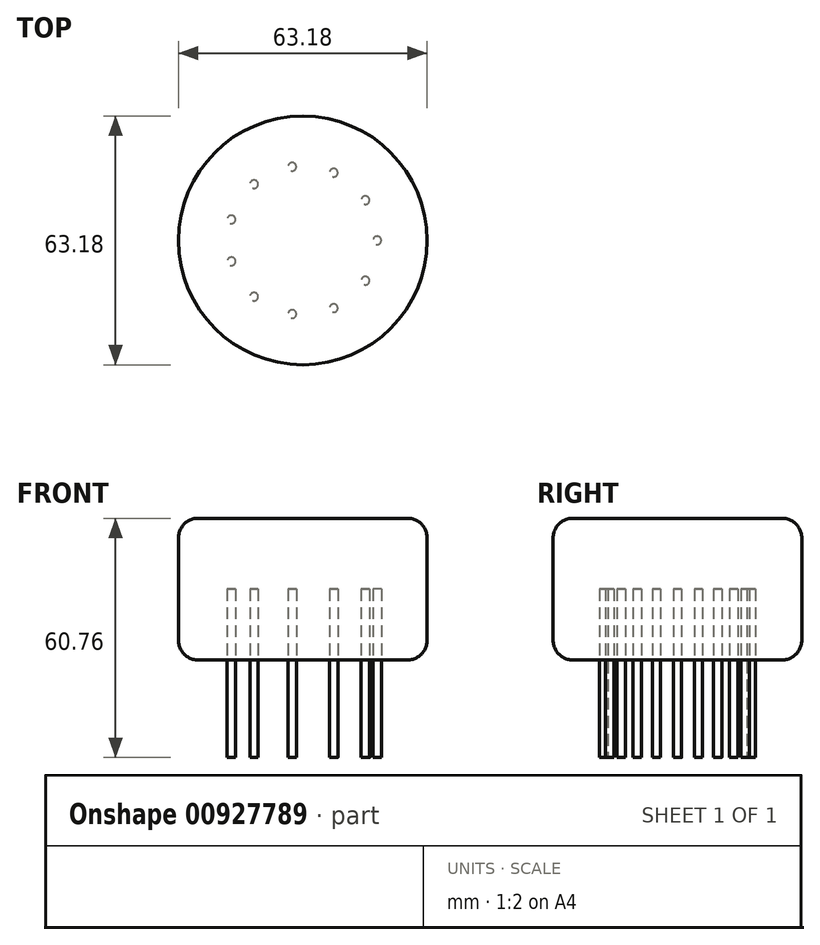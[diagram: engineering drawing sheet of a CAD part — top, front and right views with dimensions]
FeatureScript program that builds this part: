
annotation { "Feature Type Name" : "Feature", "Feature Type Description" : "" }
export const myFeature = defineFeature(function(context is Context, id is Id, definition is map)
    precondition{}
    {
        {
            var Q0;
            Q0=qCreatedBy(makeId("Front.planeOp"),FACE);
            var sketch = newSketch(context, id + "F0", { "sketchPlane" : qUnion([Q0])});
            skLineSegment(sketch, "E0", {"start": v(18.6, 87.25) * mm, "end": v(18.6, 44.5) * mm});
            skSolve(sketch);
        }
        {
            var Q0;
            Q0=qCreatedBy(makeId("Top.planeOp"),FACE);
            var Q1;
            Q1=qBodyType(qCreatedBy(id+"F2",EDGE),BodyType.WIRE);
            cPlane(context, id + "F1", {"entities" : qUnion([Q0, Q1]), "cplaneType" : CPlaneType.OFFSET, "offset" : 89 * mm, "width" : 150 * mm, "height" : 150 * mm});
        }
        {
            var Q0;
            Q0=qCreatedBy(id+"F1.planeOp",FACE);
            var sketch = newSketch(context, id + "F2", { "sketchPlane" : qUnion([Q0])});
            skCircle(sketch, "E1", {"center": v(18.9, 0) * mm, "radius": 1.05 * mm});
            skSolve(sketch);
        }
        {
            var Q0;
            Q0=qSketchRegion(id+"F2",true);
            var Q1;
            Q1=sQuery(id+"F0.wireOp",EDGE,"E0");
            var Q2;
            Q2=sQuery(id+"F0.wireOp",EDGE,"69810efb-608e-49ed-b0c7-4e798a9122e8");
            sweep(context, id + "F3", {"profiles" : qUnion([Q0]), "path" : qUnion([Q1, Q2])});
        }
        {
            var Q0;
            Q0=qCreatedBy(makeId("Front.planeOp"),FACE);
            var sketch = newSketch(context, id + "F4", { "sketchPlane" : qUnion([Q0])});
            skLineSegment(sketch, "E2", {"start": v(0, 0) * mm, "end": v(0, 88.73) * mm, "construction": true});
            skSolve(sketch);
        }
        {
            var Q0;
            Q0=makeQuery(id+"F3.opSweep","SWEPT_BODY",BODY,{"disambiguationData":[OSD([sQuery(id+"F0.wireOp",EDGE,"69810efb-608e-49ed-b0c7-4e798a9122e8"),sQuery(id+"F2.wireOp",EDGE,"E1")])]});
            var Q1;
            Q1=sQuery(id+"F4.wireOp",EDGE,"E2");
            circularPattern(context, id + "F5", {"entities" : qUnion([Q0]), "axis" : qUnion([Q1]), "angle" : 360 * degree, "instanceCount" : 11, "oppositeDirection" : true, "equalSpace" : true});
        }
        {
            var Q0;
            Q0=qCreatedBy(id+"F1.planeOp",FACE);
            var sketch = newSketch(context, id + "F6", { "sketchPlane" : qUnion([Q0])});
            skCircle(sketch, "E3", {"center": v(0, 0) * mm, "radius": 31.59 * mm});
            skCircle(sketch, "E4", {"center": v(0, 0) * mm, "radius": 11.96 * mm});
            skSolve(sketch);
        }
        {
            var Q0;
            Q0=makeQuery(id+"F6.imprint","IMPRINT",FACE,{"disambiguationData":[TD([[makeQuery(id+"F6.imprint","IMPRINT",EDGE,{"derivedFrom":sQuery(id+"F6.wireOp",EDGE,"E3")}),1.0]])]});
            var Q1;
            Q1=makeQuery(id+"F6.imprint","IMPRINT",FACE,{"disambiguationData":[TD([[makeQuery(id+"F6.imprint","IMPRINT",EDGE,{"derivedFrom":sQuery(id+"F6.wireOp",EDGE,"E4")}),1.0]])]});
            extrude(context, id + "F7", {"entities" : qUnion([Q0, Q1]), "endBound" : BoundingType.SYMMETRIC, "depth" : 36 * mm, "offsetDistance" : 25 * mm});
        }
        {
            var Q0;
            Q0=makeQuery(id+"F7.opExtrude","CAP_EDGE",EDGE,{"disambiguationData":[OSD([sQuery(id+"F6.wireOp",EDGE,"E3")])],"isStart":true});
            var Q1;
            Q1=makeQuery(id+"F7.opExtrude","CAP_EDGE",EDGE,{"disambiguationData":[OSD([sQuery(id+"F6.wireOp",EDGE,"E3")])],"isStart":false});
            fillet(context, id + "F8", {"entities" : qUnion([Q0, Q1]), "radius" : 5 * mm, "tangentPropagation" : true, "allowEdgeOverflow" : false});
        }
    });
